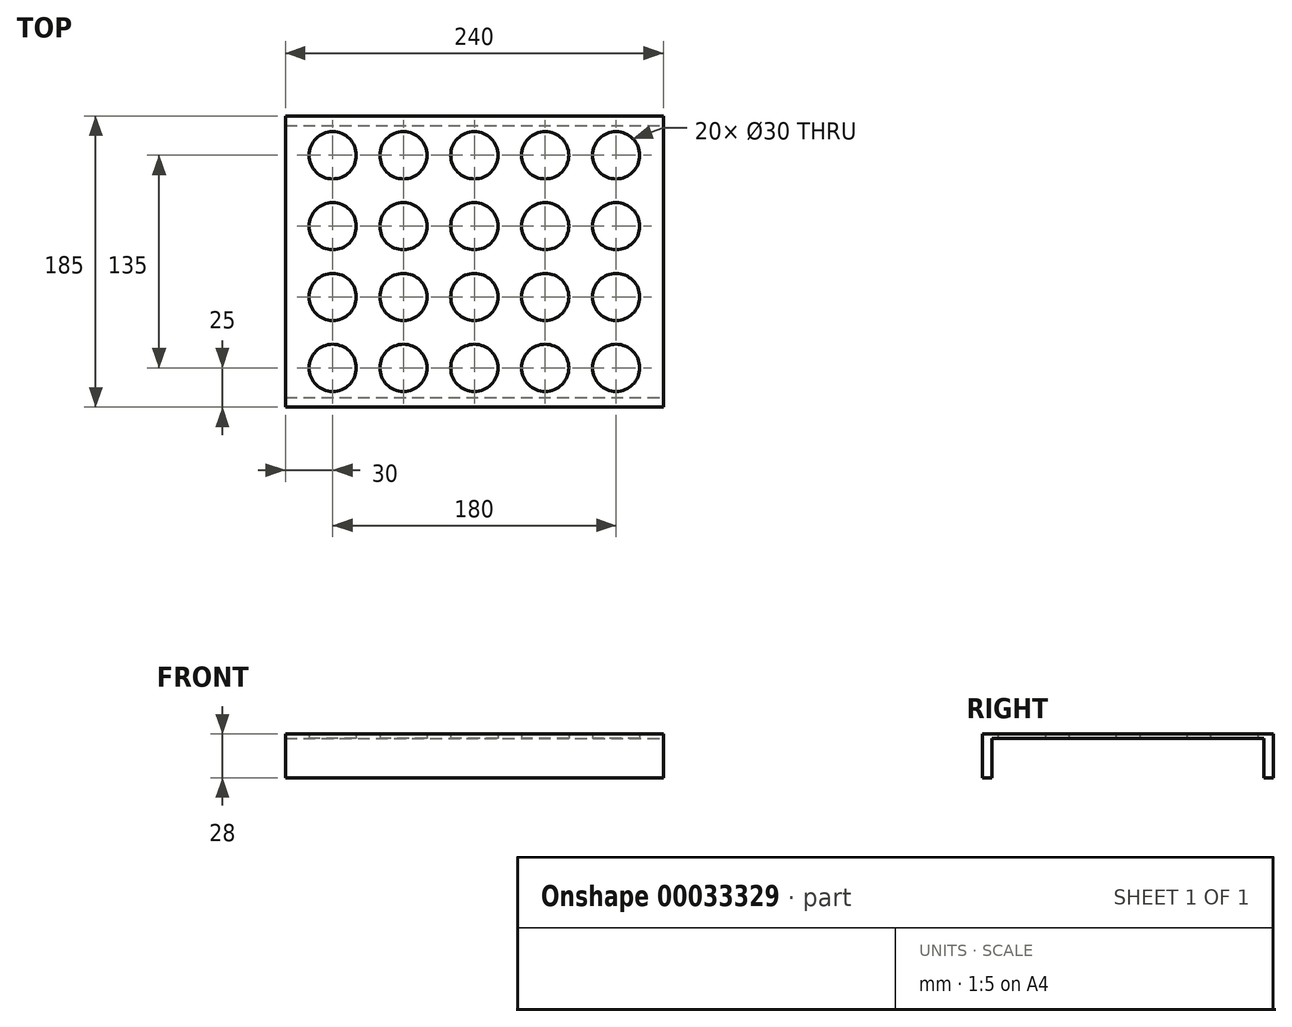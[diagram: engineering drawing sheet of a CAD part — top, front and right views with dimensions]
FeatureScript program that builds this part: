
annotation { "Feature Type Name" : "Feature", "Feature Type Description" : "" }
export const myFeature = defineFeature(function(context is Context, id is Id, definition is map)
    precondition{}
    {
        {
            var Q0;
            Q0=qCreatedBy(makeId("Top.planeOp"),FACE);
            var sketch = newSketch(context, id + "F0", { "sketchPlane" : qUnion([Q0])});
            skCircle(sketch, "E0", {"center": v(-135, -45) * mm, "radius": 15 * mm});
            skCircle(sketch, "E1.0.1.0", {"center": v(-135, 0) * mm, "radius": 15 * mm});
            skCircle(sketch, "E1.0.2.0", {"center": v(-135, 45) * mm, "radius": 15 * mm});
            skCircle(sketch, "E1.0.3.0", {"center": v(-135, 90) * mm, "radius": 15 * mm});
            skCircle(sketch, "E1.1.0.0", {"center": v(-90, -45) * mm, "radius": 15 * mm});
            skCircle(sketch, "E1.1.1.0", {"center": v(-90, 0) * mm, "radius": 15 * mm});
            skCircle(sketch, "E1.1.2.0", {"center": v(-90, 45) * mm, "radius": 15 * mm});
            skCircle(sketch, "E1.1.3.0", {"center": v(-90, 90) * mm, "radius": 15 * mm});
            skCircle(sketch, "E1.2.0.0", {"center": v(-45, -45) * mm, "radius": 15 * mm});
            skCircle(sketch, "E1.2.1.0", {"center": v(-45, 0) * mm, "radius": 15 * mm});
            skCircle(sketch, "E1.2.2.0", {"center": v(-45, 45) * mm, "radius": 15 * mm});
            skCircle(sketch, "E1.2.3.0", {"center": v(-45, 90) * mm, "radius": 15 * mm});
            skCircle(sketch, "E1.3.0.0", {"center": v(0, -45) * mm, "radius": 15 * mm});
            skCircle(sketch, "E1.3.1.0", {"center": v(0, 0) * mm, "radius": 15 * mm});
            skCircle(sketch, "E1.3.2.0", {"center": v(0, 45) * mm, "radius": 15 * mm});
            skCircle(sketch, "E1.3.3.0", {"center": v(0, 90) * mm, "radius": 15 * mm});
            skCircle(sketch, "E1.4.0.0", {"center": v(45, -45) * mm, "radius": 15 * mm});
            skCircle(sketch, "E1.4.1.0", {"center": v(45, 0) * mm, "radius": 15 * mm});
            skCircle(sketch, "E1.4.2.0", {"center": v(45, 45) * mm, "radius": 15 * mm});
            skCircle(sketch, "E1.4.3.0", {"center": v(45, 90) * mm, "radius": 15 * mm});
            skLineSegment(sketch, "E1.direction1", {"start": v(-135, -45) * mm, "end": v(-90, -45) * mm, "construction": true});
            skLineSegment(sketch, "E1.direction2", {"start": v(-135, -45) * mm, "end": v(-135, 0) * mm, "construction": true});
            skLineSegment(sketch, "E2", {"start": v(-165, 115) * mm, "end": v(75, 115) * mm});
            skLineSegment(sketch, "E3", {"start": v(75, 115) * mm, "end": v(75, -70) * mm});
            skLineSegment(sketch, "E4", {"start": v(75, -70) * mm, "end": v(-165, -70) * mm});
            skLineSegment(sketch, "E5", {"start": v(-165, -70) * mm, "end": v(-165, 115) * mm});
            skSolve(sketch);
        }
        {
            var Q0;
            Q0=makeQuery(id+"F0.imprint","IMPRINT",FACE,{"disambiguationData":[TD([[makeQuery(id+"F0.imprint","IMPRINT",EDGE,{"derivedFrom":sQuery(id+"F0.wireOp",EDGE,"E0")}),-1.0]])]});
            extrude(context, id + "F1", {"entities" : qUnion([Q0]), "depth" : 3 * mm});
        }
        {
            var Q0;
            Q0=makeQuery(id+"F1.opExtrude","CAP_FACE",FACE,{"disambiguationData":[OSD([sQuery(id+"F0.wireOp",EDGE,"E0"),sQuery(id+"F0.wireOp",EDGE,"E1.0.1.0"),sQuery(id+"F0.wireOp",EDGE,"E1.0.2.0"),sQuery(id+"F0.wireOp",EDGE,"E1.0.3.0"),sQuery(id+"F0.wireOp",EDGE,"E1.1.0.0"),sQuery(id+"F0.wireOp",EDGE,"E1.1.1.0"),sQuery(id+"F0.wireOp",EDGE,"E1.1.2.0"),sQuery(id+"F0.wireOp",EDGE,"E1.1.3.0"),sQuery(id+"F0.wireOp",EDGE,"E1.2.0.0"),sQuery(id+"F0.wireOp",EDGE,"E1.2.1.0"),sQuery(id+"F0.wireOp",EDGE,"E1.2.2.0"),sQuery(id+"F0.wireOp",EDGE,"E1.2.3.0"),sQuery(id+"F0.wireOp",EDGE,"E1.3.0.0"),sQuery(id+"F0.wireOp",EDGE,"E1.3.1.0"),sQuery(id+"F0.wireOp",EDGE,"E1.3.2.0"),sQuery(id+"F0.wireOp",EDGE,"E1.3.3.0"),sQuery(id+"F0.wireOp",EDGE,"E1.4.0.0"),sQuery(id+"F0.wireOp",EDGE,"E1.4.1.0"),sQuery(id+"F0.wireOp",EDGE,"E1.4.2.0"),sQuery(id+"F0.wireOp",EDGE,"E1.4.3.0"),sQuery(id+"F0.wireOp",EDGE,"E2"),sQuery(id+"F0.wireOp",EDGE,"E3"),sQuery(id+"F0.wireOp",EDGE,"E4"),sQuery(id+"F0.wireOp",EDGE,"E5")])],"isStart":true});
            var sketch = newSketch(context, id + "F2", { "sketchPlane" : qUnion([Q0])});
            skLineSegment(sketch, "E6.bottom", {"start": v(-165, 70) * mm, "end": v(75, 70) * mm});
            skLineSegment(sketch, "E6.top", {"start": v(-165, 64) * mm, "end": v(75, 64) * mm});
            skLineSegment(sketch, "E6.left", {"start": v(-165, 70) * mm, "end": v(-165, 64) * mm});
            skLineSegment(sketch, "E6.right", {"start": v(75, 70) * mm, "end": v(75, 64) * mm});
            skLineSegment(sketch, "E7.bottom", {"start": v(-165, -115) * mm, "end": v(75, -115) * mm});
            skLineSegment(sketch, "E7.top", {"start": v(-165, -109) * mm, "end": v(75, -109) * mm});
            skLineSegment(sketch, "E7.left", {"start": v(-165, -115) * mm, "end": v(-165, -109) * mm});
            skLineSegment(sketch, "E7.right", {"start": v(75, -115) * mm, "end": v(75, -109) * mm});
            skSolve(sketch);
        }
        {
            var Q0;
            Q0 = qSketchRegion(id + "F2", true);
            extrude(context, id + "F3", {"entities" : qUnion([Q0]), "operationType" : NewBodyOperationType.ADD, "depth" : 25 * mm});
        }
    });
